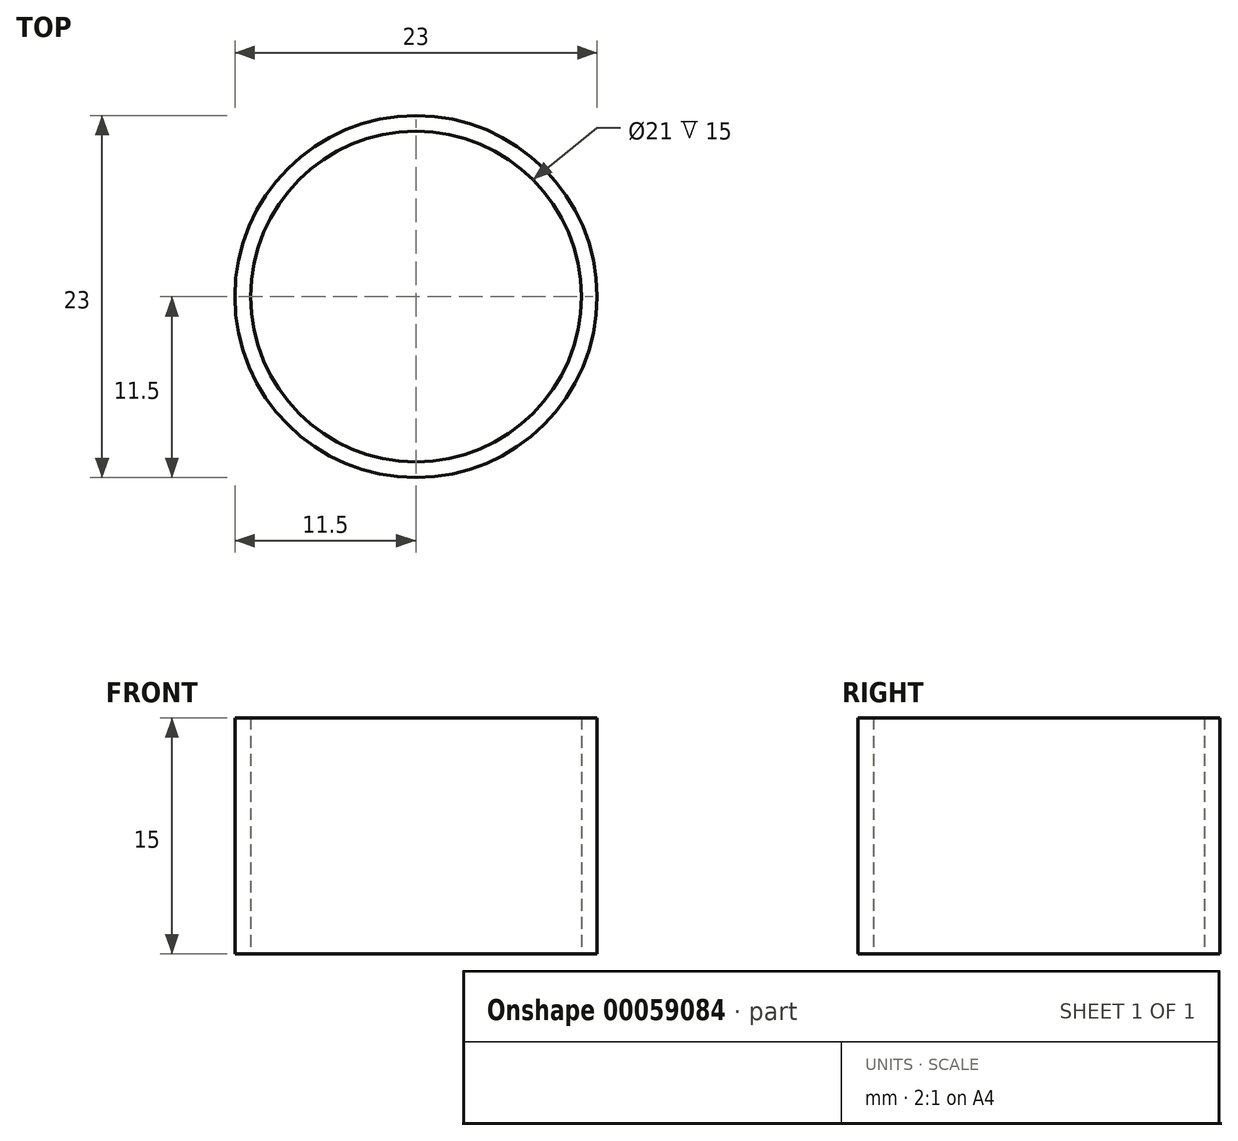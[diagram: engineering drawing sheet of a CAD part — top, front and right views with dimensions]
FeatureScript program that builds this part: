
annotation { "Feature Type Name" : "Feature", "Feature Type Description" : "" }
export const myFeature = defineFeature(function(context is Context, id is Id, definition is map)
    precondition{}
    {
        {
            var Q0;
            Q0=qCreatedBy(makeId("Top.planeOp"),FACE);
            var sketch = newSketch(context, id + "F0", { "sketchPlane" : qUnion([Q0])});
            skCircle(sketch, "E0", {"center": v(0, 0) * mm, "radius": 11.5 * mm});
            skCircle(sketch, "E1", {"center": v(0, 0) * mm, "radius": 10.5 * mm});
            skSolve(sketch);
        }
        {
            var Q0;
            Q0 = qSketchRegion(id + "F0", true);
            extrude(context, id + "F1", {"entities" : qUnion([Q0]), "depth" : 15 * mm});
        }
    });
